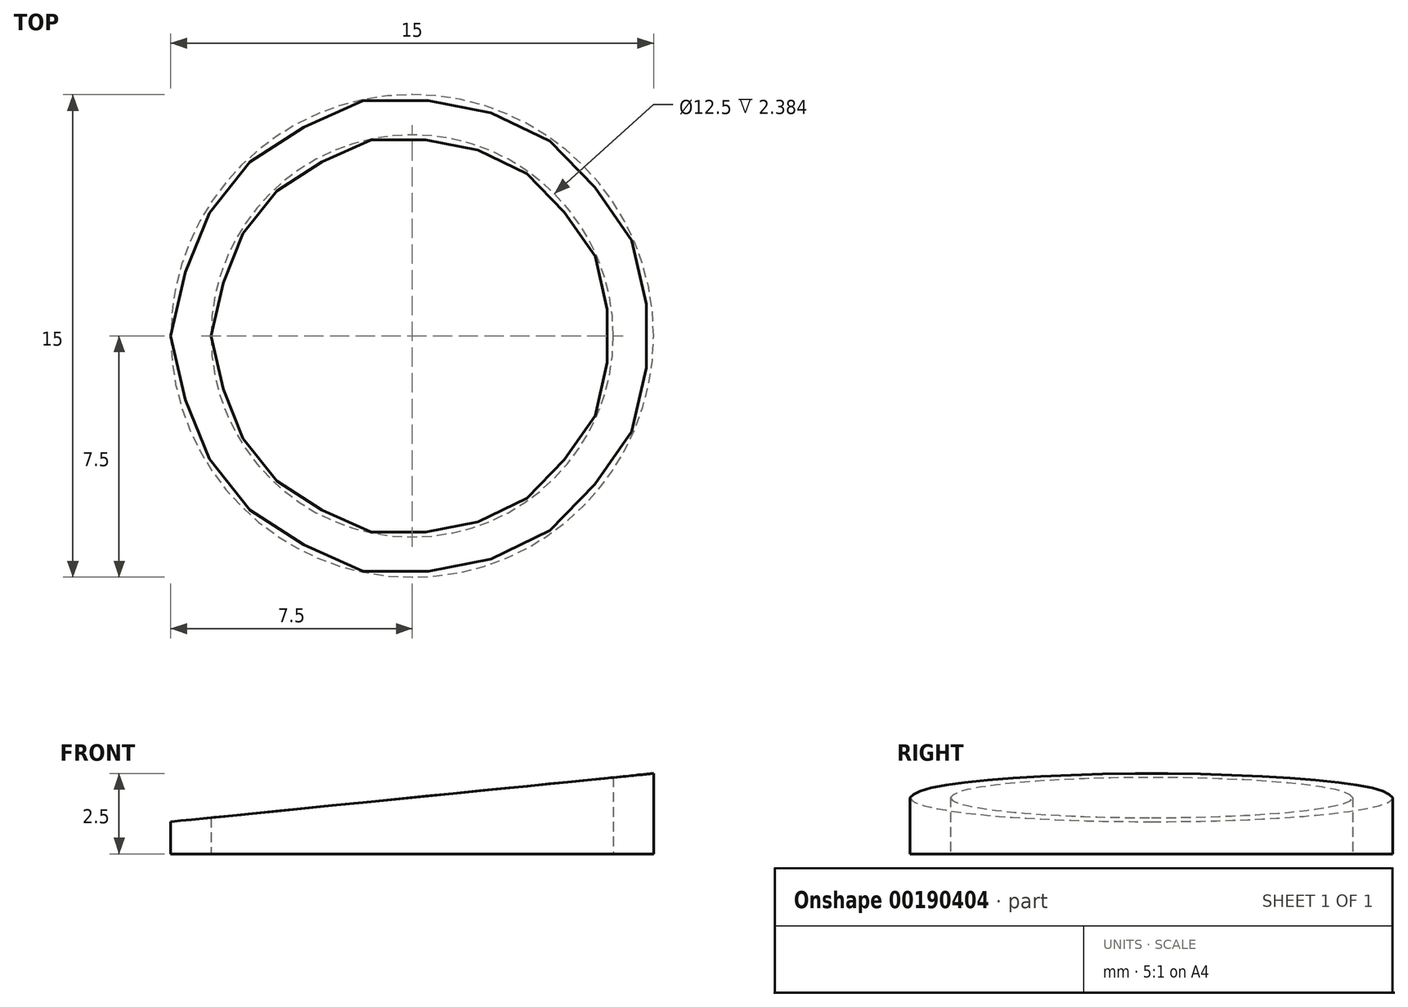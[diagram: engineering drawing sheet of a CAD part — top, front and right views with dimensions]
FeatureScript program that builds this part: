
annotation { "Feature Type Name" : "Feature", "Feature Type Description" : "" }
export const myFeature = defineFeature(function(context is Context, id is Id, definition is map)
    precondition{}
    {
        {
            var Q0;
            Q0=qCreatedBy(makeId("Top.planeOp"),FACE);
            var sketch = newSketch(context, id + "F0", { "sketchPlane" : qUnion([Q0])});
            skCircle(sketch, "E0", {"center": v(0, 0) * mm, "radius": 6.25 * mm});
            skCircle(sketch, "E1", {"center": v(0, 0) * mm, "radius": 7.5 * mm});
            skSolve(sketch);
        }
        {
            var Q0;
            Q0=makeQuery(id+"F0.imprint","IMPRINT",FACE,{"disambiguationData":[TD([[makeQuery(id+"F0.imprint","IMPRINT",EDGE,{"derivedFrom":sQuery(id+"F0.wireOp",EDGE,"E0")}),-1.0]])]});
            extrude(context, id + "F1", {"entities" : qUnion([Q0]), "depth" : 25 * mm, "offsetDistance" : 25 * mm});
        }
        {
            var Q0;
            Q0=qCreatedBy(makeId("Front.planeOp"),FACE);
            var sketch = newSketch(context, id + "F2", { "sketchPlane" : qUnion([Q0])});
            skLineSegment(sketch, "E2", {"start": v(-7.5, 0) * mm, "end": v(-7.5, 25) * mm});
            skLineSegment(sketch, "E3", {"start": v(7.5, 25) * mm, "end": v(7.5, 0) * mm});
            skLineSegment(sketch, "E4", {"start": v(-7.5, 1) * mm, "end": v(7.5, 2.5) * mm});
            skLineSegment(sketch, "E5.0", {"start": v(-7.5, 25) * mm, "end": v(7.5, 25) * mm});
            skSolve(sketch);
        }
        {
            var Q0;
            {var subQ2=sQuery(id+"F2.wireOp",EDGE,"E4");Q0=makeQuery(id+"F2.imprint","IMPRINT",FACE,{"disambiguationData":[TD([[makeQuery(id+"F2.imprint","IMPRINT",EDGE,{"derivedFrom":subQ2}),1.0]])]});}
            extrude(context, id + "F3", {"entities" : qUnion([Q0]), "operationType" : NewBodyOperationType.REMOVE, "oppositeDirection" : true, "depth" : 25 * mm, "offsetDistance" : 25 * mm, "hasSecondDirection" : true, "secondDirectionOppositeDirection" : false, "secondDirectionDepth" : 25 * mm});
        }
    });
